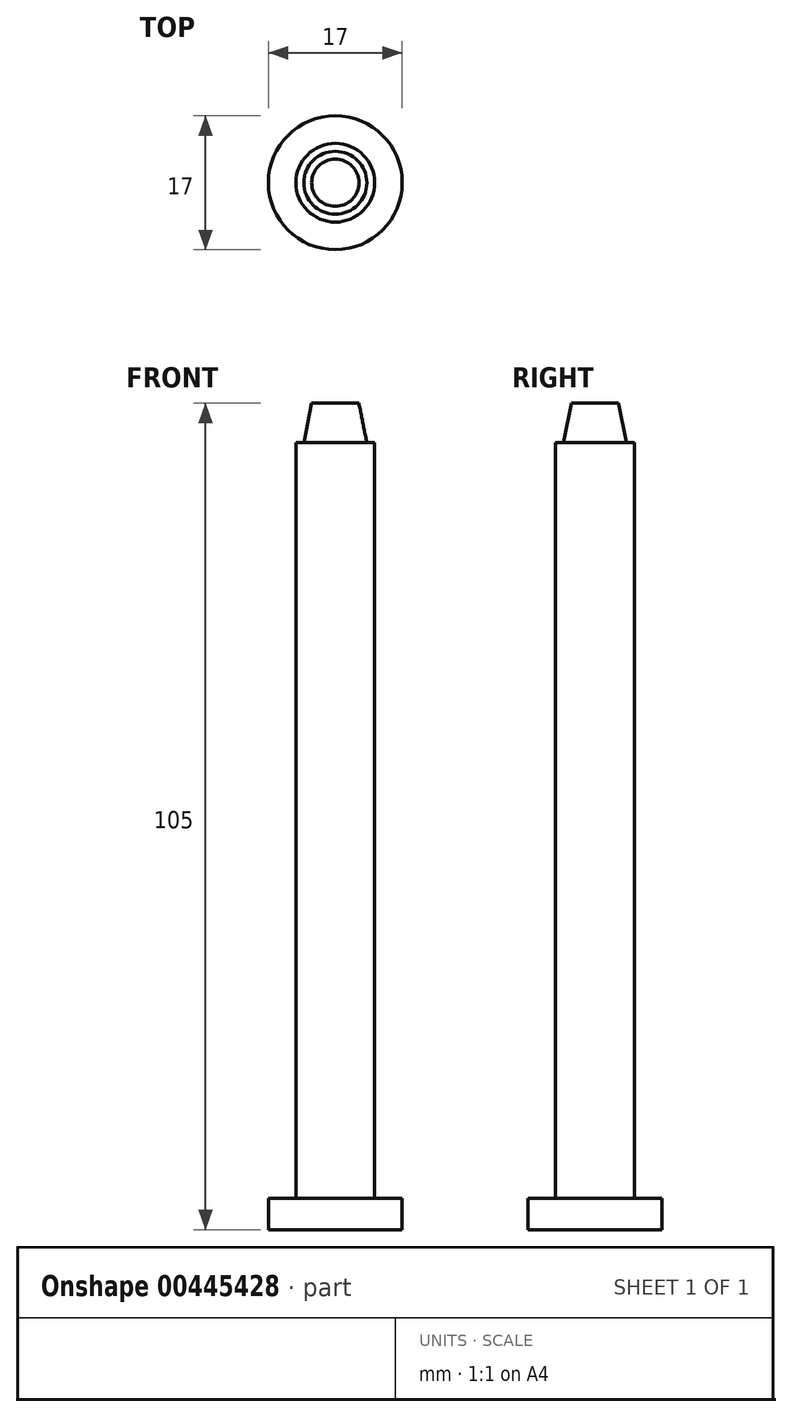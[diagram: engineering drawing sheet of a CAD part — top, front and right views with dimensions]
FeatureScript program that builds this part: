
annotation { "Feature Type Name" : "Feature", "Feature Type Description" : "" }
export const myFeature = defineFeature(function(context is Context, id is Id, definition is map)
    precondition{}
    {
        {
            var Q0;
            Q0=qCreatedBy(makeId("Top.planeOp"),FACE);
            var sketch = newSketch(context, id + "F0", { "sketchPlane" : qUnion([Q0])});
            skCircle(sketch, "E0", {"center": v(0, 0) * mm, "radius": 8.5 * mm});
            skSolve(sketch);
        }
        {
            var Q0;
            Q0 = qSketchRegion(id + "F0", true);
            extrude(context, id + "F1", {"entities" : qUnion([Q0]), "depth" : 4 * mm});
        }
        {
            var Q0;
            Q0=qCreatedBy(makeId("Top.planeOp"),FACE);
            var sketch = newSketch(context, id + "F2", { "sketchPlane" : qUnion([Q0])});
            skCircle(sketch, "E1", {"center": v(0, 0) * mm, "radius": 5 * mm});
            skSolve(sketch);
        }
        {
            var Q0;
            Q0 = qSketchRegion(id + "F2", true);
            extrude(context, id + "F3", {"entities" : qUnion([Q0]), "operationType" : NewBodyOperationType.ADD, "depth" : 100 * mm});
        }
        {
            var Q0;
            Q0=qCreatedBy(makeId("Right.planeOp"),FACE);
            var sketch = newSketch(context, id + "F4", { "sketchPlane" : qUnion([Q0])});
            skLineSegment(sketch, "E2", {"start": v(0, 105) * mm, "end": v(0, 100) * mm});
            skLineSegment(sketch, "E3", {"start": v(0, 100) * mm, "end": v(4, 100) * mm});
            skLineSegment(sketch, "E4", {"start": v(4, 100) * mm, "end": v(3, 105) * mm});
            skLineSegment(sketch, "E5", {"start": v(3, 105) * mm, "end": v(0, 105) * mm});
            skSolve(sketch);
        }
        {
            var Q0;
            Q0 = qSketchRegion(id + "F4", true);
            var Q1;
            Q1=sQuery(id+"F4.wireOp",EDGE,"E2");
            revolve(context, id + "F5", {"operationType" : NewBodyOperationType.ADD, "entities" : qUnion([Q0]), "axis" : qUnion([Q1]), "revolveType" : RevolveType.FULL});
        }
    });
